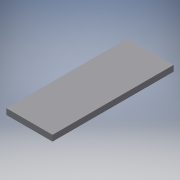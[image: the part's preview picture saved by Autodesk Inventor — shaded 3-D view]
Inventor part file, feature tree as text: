
AUTODESK INVENTOR PART (.ipt)
format: ipt  version: 2018 (Build 220112000, 112)  size: 90,624 bytes
history: native  units: mm
features: other x1, extrude x1
ambient origin geometry x8: Origin, YZ Plane, XZ Plane, XY Plane, X Axis, Y Axis, Z Axis, Center Point
bodies: Body1 (feature_tree)
feature tree (2):
  other  "Sólido1"
  extrude  "Extrusão1"  Depth=125.0mm
